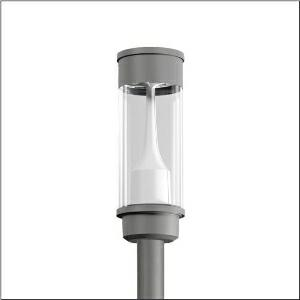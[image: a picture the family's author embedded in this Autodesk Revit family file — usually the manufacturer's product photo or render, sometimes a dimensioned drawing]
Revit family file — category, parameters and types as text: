
# Revit family: litepole_iq___st1_2a_5xa5415ef14h000022_58f2
name_source: partatom
category: Lighting Fixtures
units: mm (PartAtom-declared; Revit-internal decimal feet)

## family parameters
Cut with Voids When Loaded = No
Host = Face
Light Source = No
Part Type = Normal
Room Calculation Point = No
Round Connector Dimension = Use Diameter
Shared = No

## types (1)
- --- (1 x LED, 1540 lm, 10.5 W, 3000K)
    Apparent Load = 11 VA
    CIE Flux Codes = 22 61 93 96 100
    Color Rendering = 70
    Color Temperature = 3000K
    Default Elevation = 1800 mm
    Description = Litepole iQ, mast luminaire, Module 540 iQ-SR, primary light control with 3 zone facetted reflector, of plastic, silver coated, highly specular, structured, primary optical cover: cover, of PMMA, transparent, light distribution: ST1.2a, light emission: direct distribution, primary light characteristic: asymmetric, installation type: post-top, LED, High Power LED, rated luminous flux: 1.540lm, luminous efficacy: 147lm/W, light colour: 730, colour temperature: 3000K, control gear: iQ Street-Remote, control: Street-Remote, Auto-Match, Temp-Guard, Lumen-Switch, Night-Set, Smart-Wire, Light-Fading, Desk-Remote (wireless, voltage-free reading and setting of iQ features in the workshop via application-optimized NFC function/RFID function), optimised constant luminous flux control (CLO 2.0), pre-setting: logarithmic dimming characteristic, mains connection: 230..240V, AC, 50/60Hz, connection cable pre-assembled, cable length: 5,5m, wiring characteristics: H07RN-F, start of lifetime: 11W, end of service life: 11W, reduction: 5W, luminaire housing, upper part, of glass-fibre reinforced polyester, coated, SITECO metallic grey (DB 702S), diameter: 210mm, height: 590mm, spigot size: d x l = 76 x 70mm (post-top) | with reducer (optional accessory) 60 x 70mm, mounting height: 3..5m, post-top mast mounting element, of diecast aluminium, coated, SITECO metallic grey (DB 702S), Module 540 iQ-SR, traffic white (RAL 9016), equipment: standard, protection rating (complete): IP65, insulation class (complete): insulation class II (safety insulation), certification: CE, ENEC, VDE, packaging unit: 1 piece

Light Distribution: ST1.2a
    Height = 590 mm
    Lamp = 1 x LED
    Lamp Light Flux = 1540 lm
    Lamp Power = 10.5 W
    Lamp count = 1
    Length = 220 mm
    Luminous efficacy = 147 lm/W
    Manufacturer = Siteco
    ModVariant = No
    Model = 5XA5415EF14H000022
    Number of Poles = 1
    OnlyDefault = Yes
    Power Factor = 1
    Product Name = Litepole iQ | ST1.2a
    Product group = mast luminaire | pylon top
    ProductGroupID = 6100
    Protection Class = Protection class II
    Protection Degree = IP 65
    RLX_Detail_Level = 1
    RLX_Emergency_Light_Flux = 0 lm
    RLX_Emergency_Type = 0
    RLX_Emergency_Type_DB = No
    RlxData = <blob elided: 41385 chars, md5=700e8f8d>
    Socket = socket
    Standby Power = 0 W
    System Light Flux = 1540 lm
    System Power = 11 W
    Type Comments = factory setting: luminous flux: 100 % | dim-lin: 254 | 419 mA
    Type Image = l_1006025.jpg
    URL = http://relux.com
    VarID = @adj_158273
    Voltage = 0 V
    Weight = 0.00 kg
    Width = 0 mm  [stored 0 ft]

note: [stored X ft] marks values corroborated as IEEE doubles in the binary element streams (Revit-internal decimal feet)

## geometry (parser evidence)
native form markers: Blend x4, Sweep x10
no freeform markers — native parametric forms only
